# Revit family: Lighting_Ceiling-Mounted_Reggiani_EVO-43mm-Precision
name_source: partatom
category: Modelli generici
revit_build: Autodesk Revit 2016 (Build: 20150220_1215(x64)
units: mm (PartAtom-declared; Revit-internal decimal feet)

## family parameters
Condiviso = No
Host = Superficie
Punto di calcolo locali = No
Può ospitare armatura = No
Quota connettore circolare = Usa diametro
Taglio con vuoti quando caricato = No
Tipo di parte = Normale

## types (2) — shared parameters
BIMobject category = Ceiling Mounted
BIMobject category code = lighting-ceiling-mounted
BIMobject main category = Lighting
BIMobject main category code = lighting
Brand url = http://www.reggiani.net
Design country = Italy
Edition number = 1
IFC Classification = Light Fixture
Installation instructions = http://www.reggiani.net
Manufacturer country = Italy
Manufacturer name = Reggiani
Material main = Aluminium
NBS Reference Code = 70-50-46
NBS Reference Description = Lighting Tracks
Nominal height = 71 mm  [stored 0.23294 ft]
Nominal width = 43 mm  [stored 0.141076 ft]
OmniClass Code = 23-35 47 21 17
OmniClass Description = Lighting Tracks
Product Guid = cf014bb7-0a47-425b-9187-04f9788f6f74
Product SKU = yori_evo_box_43-precision
Product certification = http://www.reggiani.net
Product data url = https://bimobject.com
Product family = Track fixture
Product group = Yori
Product url = http://www.reggiani.net
Produttore = Reggiani Spa Illuminazione
Viale Monza 16, 
20845 Sovico (MB) Italia
Prospetto di default = 1219 mm
QR code = http://bimobject.com
Technical description = http://www.reggiani.net Brochure_Mains Voltage (10).pdf
UNSPSC Code = 3911
URL = http://www.reggiani.net
Uniclass 1.4 Code = L747363
Uniclass 1.4 Description = Lighting track
Uniclass 2.0 Code = PR-70-50-46
Uniclass 2.0 Description = Lighting Tracks
Uniclass 2015 Code = Pr_70_70_48_47
Uniclass 2015 Name = Lighting tracks
Weight Net (Kg) = 0.5
body = Reggiani Alluminio  white

## per-type parameters (varying)
| type | Rotation oriz |
| Reggiani EVO  Ø 43mm  Perecision- mod FH81 B- E-H | 40.00° |
| Reggiani EVO  Ø 43mm  Perecision- mod FH82 B- E-H | 90.00° |

note: column(s) folded — value = type name in every type: Modello

note: [stored X ft] marks values corroborated as IEEE doubles in the binary element streams (Revit-internal decimal feet)
